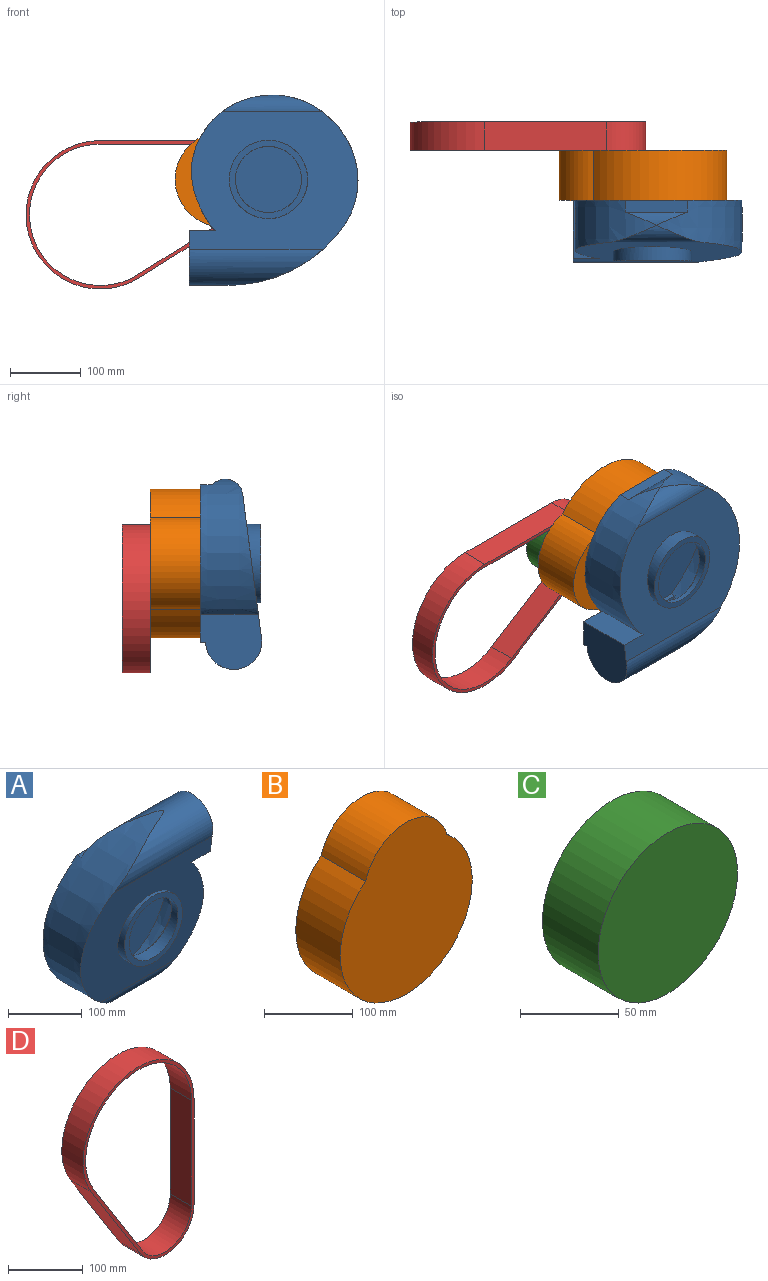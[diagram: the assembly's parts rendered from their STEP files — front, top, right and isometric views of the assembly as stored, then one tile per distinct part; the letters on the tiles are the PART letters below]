
ASSEMBLY  parts=4 mates=3
PART A: 29 faces, bbox 240.7x87x269.2 mm
  f0: plane 87x77.88mm, normal (1,0,0), area 5718.3mm2, adj f3,f4,f5,f7,f8
  f1: extruded ~269.24x182.46mm, area 27049.8mm2, adj f4,f5,f6,f7,f8,f9,f10
  f2: extruded ~191.36x114.78mm, area 16169.1mm2, adj f3,f4,f5,f6,f9,f10
  f3: plane 81.86x37.49mm, normal (0,0,-1), area 3069.1mm2, adj f0,f2,f4,f5
  f4: plane 240.68x227.16mm, normal (0,1,0), area 44985.7mm2, adj f0,f1,f2,f3,f8,f10
  f5: plane 238.58x194.54mm, normal (0,-0.99,-0.13), area 31443.5mm2, adj f0,f1,f2,f3,f6,f7,f12
  f6: cylinder r=24.76mm len=141.6mm, axis (1,0,0), area 2879.2mm2, adj f1,f2,f5
  f7: cylinder r=39.88mm len=189.34mm, axis (1,0,0), area 16777.1mm2, adj f0,f1,f5,f8
  f8: plane 173x7.28mm, normal (0,0,1), area 1258.6mm2, adj f0,f1,f4,f7
  f9: cylinder r=24.76mm len=87.45mm, axis (1,0,0), area 933.5mm2, adj f1,f2,f10
  f10: plane 87.45x16.8mm, normal (0,0,-1), area 1469mm2, adj f1,f2,f4,f9
  f11: cylinder r=46.83mm len=93.65mm, axis (0,1,0), area 3690.6mm2, adj f13,f14
  f12: cylinder r=55.48mm len=110.96mm, axis (0,1,0), area 4372.8mm2, adj f5,f13
  f13: plane 110.96x110.96mm, normal (0,-1,0), area 2782mm2, adj f11,f12
  f14: plane 101.65x101.65mm, normal (0,0.99,0.13), area 1237.5mm2, adj f11,f26
  f15: plane 79x69.88mm, normal (-1,0,0), area 4611.4mm2, adj f18,f19,f20,f22,f23
  f16: extruded ~261.23x178.5mm, area 23588.6mm2, adj f19,f20,f21,f22,f23,f24,f25
  f17: extruded ~191.36x110.72mm, area 14664.1mm2, adj f18,f19,f20,f21,f24,f25
  f18: plane 74.35x45.66mm, normal (0,0,1), area 3394.9mm2, adj f15,f17,f19,f20
  f19: plane 230.58x214.7mm, normal (0,-1,0), area 41662.4mm2, adj f15,f16,f17,f18,f23,f25
  f20: plane 230.58x195.02mm, normal (0,0.99,0.13), area 30928.6mm2, adj f15,f16,f17,f18,f21,f22,f27
  f21: cylinder r=20.76mm len=128.93mm, axis (1,0,0), area 2201.5mm2, adj f16,f17,f20
  f22: cylinder r=35.88mm len=178.19mm, axis (1,0,0), area 14711.7mm2, adj f15,f16,f20,f23
  f23: plane 167.71x7.33mm, normal (0,0,-1), area 1229.1mm2, adj f15,f16,f19,f22
  f24: cylinder r=20.76mm len=85.92mm, axis (1,0,0), area 848mm2, adj f16,f17,f25
  f25: plane 85.92x14.68mm, normal (0,0,1), area 1261mm2, adj f16,f17,f19,f24
  f26: cylinder r=50.83mm len=101.65mm, axis (0,1,0), area 2728.4mm2, adj f14,f28
  f27: cylinder r=51.48mm len=102.96mm, axis (0,1,0), area 4068.5mm2, adj f20,f28
  f28: plane 102.96x102.96mm, normal (0,1,0), area 210.7mm2, adj f26,f27
PART B: 4 faces, bbox 210.5x71x237.3 mm
  f0: cylinder r=67.37mm len=129.69mm, axis (0,-1,0), area 12399.7mm2, adj f1,f2,f3
  f1: cylinder r=105.26mm len=210.52mm, axis (0,-1,0), area 37036.6mm2, adj f0,f2,f3
  f2: plane 237.27x210.52mm, normal (0,1,0), area 37528.7mm2, adj f0,f1
  f3: plane 237.27x210.52mm, normal (0,-1,0), area 37528.7mm2, adj f0,f1
PART C: 3 faces, bbox 100x40x100 mm
  f0: cylinder r=50mm len=100mm, axis (0,-1,0), area 12566.4mm2, adj f1,f2
  f1: plane 100x100mm, normal (0,1,0), area 7854mm2, adj f0
  f2: plane 100x100mm, normal (0,-1,0), area 7854mm2, adj f0
PART D: 10 faces, bbox 210x40x333.4 mm
  f0: cylinder r=105mm len=210mm, axis (0,-1,0), area 15552.6mm2, adj f1,f7,f8,f9
  f1: plane 173.42x40mm, normal (1,0,0), area 6936.9mm2, adj f0,f2,f8,f9
  f2: cylinder r=55mm len=101.56mm, axis (0,-1,0), area 5676.4mm2, adj f1,f7,f8,f9
  f3: cylinder r=50mm len=92.33mm, axis (0,-1,0), area 5160.4mm2, adj f4,f6,f8,f9
  f4: plane 173.42x40mm, normal (-1,0,0), area 6936.9mm2, adj f3,f5,f8,f9
  f5: cylinder r=100mm len=200mm, axis (0,-1,0), area 14812mm2, adj f4,f6,f8,f9
  f6: plane 146.8x92.33mm, normal (0.85,0,0.53), area 6936.9mm2, adj f3,f5,f8,f9
  f7: plane 146.8x92.33mm, normal (-0.85,0,-0.53), area 6936.9mm2, adj f0,f2,f8,f9
  f8: plane 333.42x210mm, normal (0,1,0), area 4309.3mm2, adj f0,f1,f2,f3,f4,f5,f6,f7
  f9: plane 333.42x210mm, normal (0,-1,0), area 4309.3mm2, adj f0,f1,f2,f3,f4,f5,f6,f7
PLACE A rot(axis=(0,1,0),180deg) t=(0,-71,0)mm
PLACE B rot(axis=(0,-1,0),90deg) t=(0,-71,0)mm
PLACE C t=(-64.64,-71,-64.64)mm
PLACE D rot(axis=(0,-1,0),90deg) t=(0,-71,0)mm
MATE fastened C.f0 <-> B.f0  axis (0,-1,0) through (-64.64,0,0)mm
MATE fastened D.f3 <-> C.f0  axis (0,-1,0) through (-64.64,40,0)mm
MATE fastened A.f12 <-> B.f1  axis (0,-1,0) through (0,-156,0)mm
